# Revit family: ЭВАН ЭПВН 72-120 кВт
name_source: partatom
category: Оборудование
units: mm (PartAtom-declared; Revit-internal decimal feet)

## family parameters
Всегда вертикально = Да
Классификация = Нет
На основе рабочей плоскости = Да
Общий = Нет
При загрузке вырезать с полостями = Нет
Размер круглого соединителя = Использовать диаметр
Тип детали = Нормальный
Точка расчета площади = Нет

## types (5) — shared parameters
ADSK_Классификация нагрузок = Прочее
ADSK_Количество фаз = 3
ADSK_Материал = Сталь
ADSK_Номинальная мощность = 0 Вт
ADSK_Размер_Высота = 590 мм
ADSK_Размер_Длина = 1392 мм
ADSK_Размер_Ширина = 469 мм
Dn = 20 мм
База = ЭЛЕКТРИЧЕСКИЙ ТЕПЛОГЕНЕРАТОР (КОТЕЛ)
Крышка_Видимость = Да
Максимальная температура теплоносителя, оС = +68
Материал корпуса = Сталь
Минимально допустимое давление допустимое на входе в водонагреватель, МПа = 0.02
Мощность 1-й ступени (по умолчанию) = 0 Вт
Объем колбы котла, л = 80
Рабоча зона_Видимость = Да
Резьба патрубков для подключения трубопроводов теплоносителя = G 3/4
zero-valued in all types: Отметка по умолчанию

## per-type parameters (varying)
| type | ADSK_Расход теплоносителя | Потребляемая электрическая мощность при максимальной тепловой мощность  в час, кВт/ч |
| ЭВАН ЭПВН - 72 кВт | 1.8 м³/ч | 75.6 |
| ЭВАН ЭПВН - 84 кВт | 2.1 м³/ч | 88.2 |
| ЭВАН ЭПВН - 96 кВт | 2.4 м³/ч | 100.8 |
| ЭВАН ЭПВН - 108 кВт | 2.7 м³/ч | 113.4 |
| ЭВАН ЭПВН - 120 кВт | 3.0 м³/ч | 126 |
